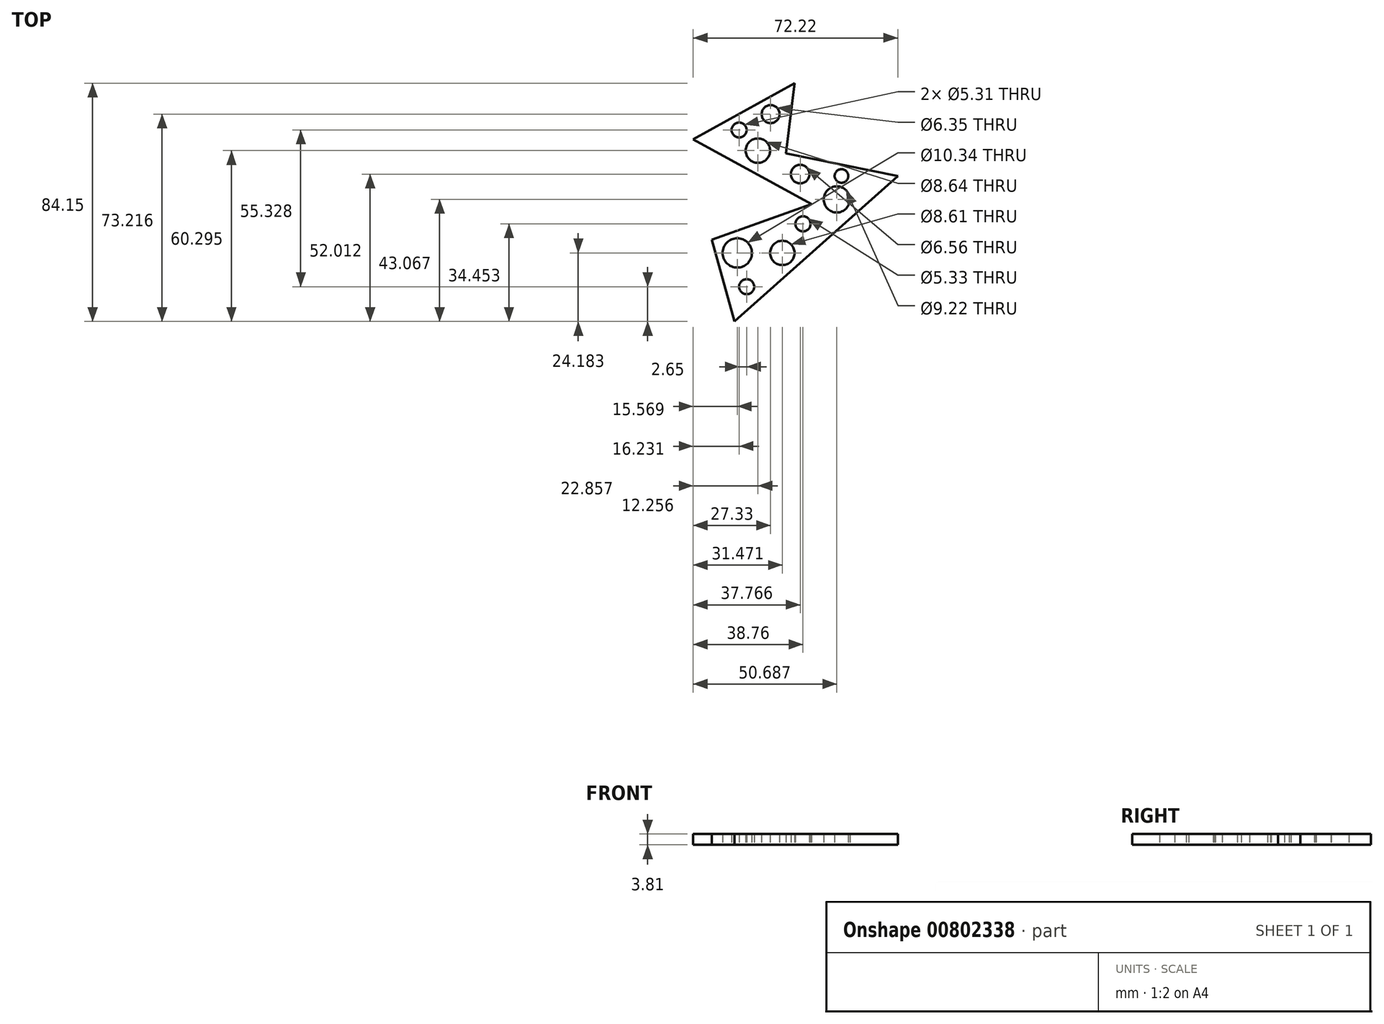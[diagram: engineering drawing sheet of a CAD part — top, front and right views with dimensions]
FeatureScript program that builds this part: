
annotation { "Feature Type Name" : "Feature", "Feature Type Description" : "" }
export const myFeature = defineFeature(function(context is Context, id is Id, definition is map)
    precondition{}
    {
        {
            var Q0;
            Q0=qCreatedBy(makeId("Top.planeOp"),FACE);
            var sketch = newSketch(context, id + "F0", { "sketchPlane" : qUnion([Q0])});
            skLineSegment(sketch, "E0", {"start": v(8.45, 37.77) * mm, "end": v(-27.33, 17.9) * mm});
            skLineSegment(sketch, "E1", {"start": v(8.45, 37.77) * mm, "end": v(5.47, 12.92) * mm});
            skLineSegment(sketch, "E2", {"start": v(5.47, 12.92) * mm, "end": v(44.9, 4.97) * mm});
            skLineSegment(sketch, "E3", {"start": v(44.9, 4.97) * mm, "end": v(-12.76, -46.38) * mm});
            skLineSegment(sketch, "E4", {"start": v(-27.33, 17.9) * mm, "end": v(14.41, -4.97) * mm});
            skLineSegment(sketch, "E5", {"start": v(14.41, -4.97) * mm, "end": v(-20.7, -17.56) * mm});
            skLineSegment(sketch, "E6", {"start": v(-20.7, -17.56) * mm, "end": v(-12.76, -46.38) * mm});
            skCircle(sketch, "E7", {"center": v(-11.1, 21.2) * mm, "radius": 2.65 * mm});
            skCircle(sketch, "E8", {"center": v(0, 26.84) * mm, "radius": 3.18 * mm});
            skCircle(sketch, "E9", {"center": v(25.01, 4.97) * mm, "radius": 2.41 * mm});
            skCircle(sketch, "E10", {"center": v(-11.76, -22.2) * mm, "radius": 5.17 * mm});
            skCircle(sketch, "E11", {"center": v(-4.47, 13.91) * mm, "radius": 4.32 * mm});
            skCircle(sketch, "E12", {"center": v(4.14, -22.2) * mm, "radius": 4.3 * mm});
            skCircle(sketch, "E13", {"center": v(-8.45, -34.12) * mm, "radius": 2.65 * mm});
            skCircle(sketch, "E14", {"center": v(10.44, 5.63) * mm, "radius": 3.28 * mm});
            skCircle(sketch, "E15", {"center": v(11.43, -11.93) * mm, "radius": 2.67 * mm});
            skCircle(sketch, "E16", {"center": v(23.36, -3.31) * mm, "radius": 4.61 * mm});
            skSolve(sketch);
        }
        {
            var Q0;
            Q0 = qSketchRegion(id + "F0", true);
            extrude(context, id + "F1", {"entities" : qUnion([Q0]), "depth" : 3.8 * mm, "offsetDistance" : 25.4 * mm});
        }
    });
